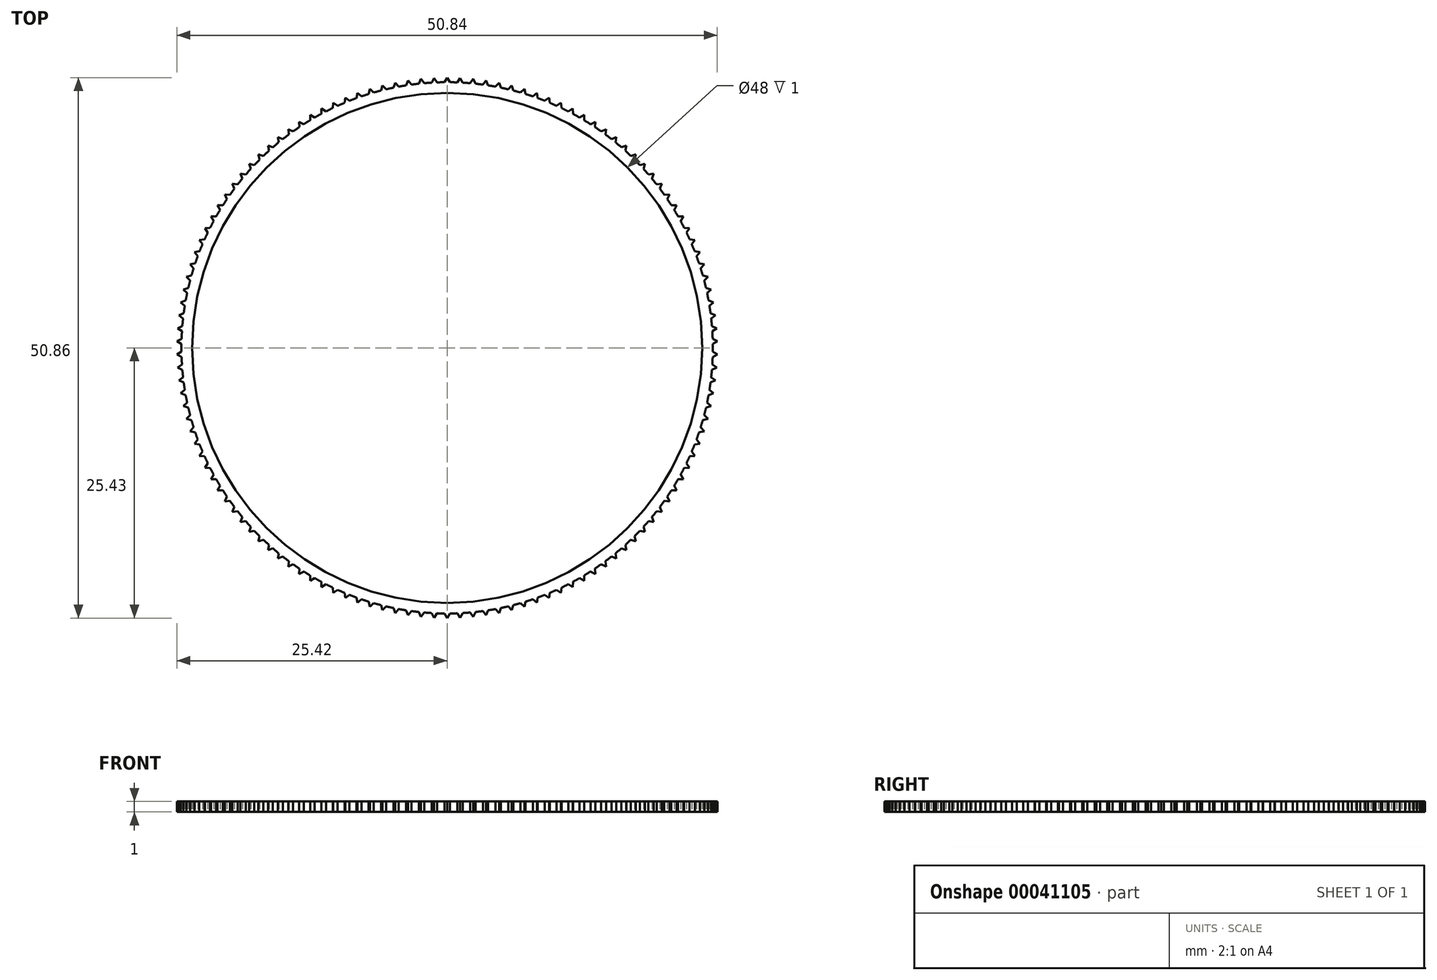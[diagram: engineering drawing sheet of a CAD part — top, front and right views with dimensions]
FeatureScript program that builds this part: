
annotation { "Feature Type Name" : "Feature", "Feature Type Description" : "" }
export const myFeature = defineFeature(function(context is Context, id is Id, definition is map)
    precondition{}
    {
        {
            var Q0;
            Q0=qCreatedBy(makeId("Top.planeOp"),FACE);
            var sketch = newSketch(context, id + "F0", { "sketchPlane" : qUnion([Q0])});
            skCircle(sketch, "E0", {"center": v(0, 0) * mm, "radius": 25 * mm});
            skLineSegment(sketch, "E1", {"start": v(0, 33.72) * mm, "end": v(0, -40.04) * mm, "construction": true});
            skLineSegment(sketch, "E2", {"start": v(-0.25, -25) * mm, "end": v(0, -25.43) * mm});
            skLineSegment(sketch, "E3", {"start": v(0, -25.43) * mm, "end": v(0.25, -25) * mm});
            skLineSegment(sketch, "E4", {"start": v(-0.25, -25) * mm, "end": v(0.25, -25) * mm, "construction": true});
            skLineSegment(sketch, "E5.1.0", {"start": v(0.96, -24.98) * mm, "end": v(1.23, -25.4) * mm});
            skLineSegment(sketch, "E5.1.1", {"start": v(1.23, -25.4) * mm, "end": v(1.46, -24.96) * mm});
            skLineSegment(sketch, "E5.2.0", {"start": v(2.16, -24.9) * mm, "end": v(2.45, -25.31) * mm});
            skLineSegment(sketch, "E5.2.1", {"start": v(2.45, -25.31) * mm, "end": v(2.66, -24.86) * mm});
            skLineSegment(sketch, "E5.3.0", {"start": v(3.36, -24.77) * mm, "end": v(3.67, -25.16) * mm});
            skLineSegment(sketch, "E5.3.1", {"start": v(3.67, -25.16) * mm, "end": v(3.86, -24.7) * mm});
            skLineSegment(sketch, "E5.4.0", {"start": v(4.56, -24.58) * mm, "end": v(4.89, -24.96) * mm});
            skLineSegment(sketch, "E5.4.1", {"start": v(4.89, -24.96) * mm, "end": v(5.05, -24.48) * mm});
            skLineSegment(sketch, "E5.5.0", {"start": v(5.74, -24.33) * mm, "end": v(6.09, -24.7) * mm});
            skLineSegment(sketch, "E5.5.1", {"start": v(6.09, -24.7) * mm, "end": v(6.23, -24.21) * mm});
            skLineSegment(sketch, "E5.6.0", {"start": v(6.9, -24.03) * mm, "end": v(7.27, -24.37) * mm});
            skLineSegment(sketch, "E5.6.1", {"start": v(7.27, -24.37) * mm, "end": v(7.39, -23.88) * mm});
            skLineSegment(sketch, "E5.7.0", {"start": v(8.06, -23.66) * mm, "end": v(8.44, -24) * mm});
            skLineSegment(sketch, "E5.7.1", {"start": v(8.44, -24) * mm, "end": v(8.53, -23.5) * mm});
            skLineSegment(sketch, "E5.8.0", {"start": v(9.2, -23.25) * mm, "end": v(9.6, -23.55) * mm});
            skLineSegment(sketch, "E5.8.1", {"start": v(9.6, -23.55) * mm, "end": v(9.66, -23.06) * mm});
            skLineSegment(sketch, "E5.9.0", {"start": v(10.3, -22.78) * mm, "end": v(10.72, -23.06) * mm});
            skLineSegment(sketch, "E5.9.1", {"start": v(10.72, -23.06) * mm, "end": v(10.76, -22.57) * mm});
            skLineSegment(sketch, "E5.10.0", {"start": v(11.4, -22.25) * mm, "end": v(11.82, -22.52) * mm});
            skLineSegment(sketch, "E5.10.1", {"start": v(11.82, -22.52) * mm, "end": v(11.84, -22.02) * mm});
            skLineSegment(sketch, "E5.11.0", {"start": v(12.46, -21.67) * mm, "end": v(12.9, -21.92) * mm});
            skLineSegment(sketch, "E5.11.1", {"start": v(12.9, -21.92) * mm, "end": v(12.89, -21.42) * mm});
            skLineSegment(sketch, "E5.12.0", {"start": v(13.5, -21.05) * mm, "end": v(13.94, -21.27) * mm});
            skLineSegment(sketch, "E5.12.1", {"start": v(13.94, -21.27) * mm, "end": v(13.9, -20.77) * mm});
            skLineSegment(sketch, "E5.13.0", {"start": v(14.5, -20.37) * mm, "end": v(14.95, -20.57) * mm});
            skLineSegment(sketch, "E5.13.1", {"start": v(14.95, -20.57) * mm, "end": v(14.9, -20.08) * mm});
            skLineSegment(sketch, "E5.14.0", {"start": v(15.46, -19.65) * mm, "end": v(15.92, -19.83) * mm});
            skLineSegment(sketch, "E5.14.1", {"start": v(15.92, -19.83) * mm, "end": v(15.85, -19.33) * mm});
            skLineSegment(sketch, "E5.15.0", {"start": v(16.4, -18.88) * mm, "end": v(16.86, -19.04) * mm});
            skLineSegment(sketch, "E5.15.1", {"start": v(16.86, -19.04) * mm, "end": v(16.76, -18.55) * mm});
            skLineSegment(sketch, "E5.16.0", {"start": v(17.28, -18.06) * mm, "end": v(17.76, -18.2) * mm});
            skLineSegment(sketch, "E5.16.1", {"start": v(17.76, -18.2) * mm, "end": v(17.64, -17.71) * mm});
            skLineSegment(sketch, "E5.17.0", {"start": v(18.14, -17.2) * mm, "end": v(18.62, -17.32) * mm});
            skLineSegment(sketch, "E5.17.1", {"start": v(18.62, -17.32) * mm, "end": v(18.48, -16.84) * mm});
            skLineSegment(sketch, "E5.18.0", {"start": v(18.95, -16.31) * mm, "end": v(19.44, -16.4) * mm});
            skLineSegment(sketch, "E5.18.1", {"start": v(19.44, -16.4) * mm, "end": v(19.27, -15.93) * mm});
            skLineSegment(sketch, "E5.19.0", {"start": v(19.71, -15.38) * mm, "end": v(20.2, -15.44) * mm});
            skLineSegment(sketch, "E5.19.1", {"start": v(20.2, -15.44) * mm, "end": v(20.02, -14.98) * mm});
            skLineSegment(sketch, "E5.20.0", {"start": v(20.43, -14.4) * mm, "end": v(20.93, -14.45) * mm});
            skLineSegment(sketch, "E5.20.1", {"start": v(20.93, -14.45) * mm, "end": v(20.72, -14) * mm});
            skLineSegment(sketch, "E5.21.0", {"start": v(21.1, -13.4) * mm, "end": v(21.6, -13.42) * mm});
            skLineSegment(sketch, "E5.21.1", {"start": v(21.6, -13.42) * mm, "end": v(21.37, -12.98) * mm});
            skLineSegment(sketch, "E5.22.0", {"start": v(21.73, -12.37) * mm, "end": v(22.23, -12.36) * mm});
            skLineSegment(sketch, "E5.22.1", {"start": v(22.23, -12.36) * mm, "end": v(21.97, -11.93) * mm});
            skLineSegment(sketch, "E5.23.0", {"start": v(22.3, -11.3) * mm, "end": v(22.8, -11.27) * mm});
            skLineSegment(sketch, "E5.23.1", {"start": v(22.8, -11.27) * mm, "end": v(22.52, -10.86) * mm});
            skLineSegment(sketch, "E5.24.0", {"start": v(22.82, -10.21) * mm, "end": v(23.32, -10.16) * mm});
            skLineSegment(sketch, "E5.24.1", {"start": v(23.32, -10.16) * mm, "end": v(23.02, -9.75) * mm});
            skLineSegment(sketch, "E5.25.0", {"start": v(23.29, -9.1) * mm, "end": v(23.78, -9.02) * mm});
            skLineSegment(sketch, "E5.25.1", {"start": v(23.78, -9.02) * mm, "end": v(23.46, -8.63) * mm});
            skLineSegment(sketch, "E5.26.0", {"start": v(23.7, -7.96) * mm, "end": v(24.19, -7.86) * mm});
            skLineSegment(sketch, "E5.26.1", {"start": v(24.19, -7.86) * mm, "end": v(23.85, -7.49) * mm});
            skLineSegment(sketch, "E5.27.0", {"start": v(24.06, -6.8) * mm, "end": v(24.54, -6.68) * mm});
            skLineSegment(sketch, "E5.27.1", {"start": v(24.54, -6.68) * mm, "end": v(24.19, -6.33) * mm});
            skLineSegment(sketch, "E5.28.0", {"start": v(24.36, -5.64) * mm, "end": v(24.83, -5.49) * mm});
            skLineSegment(sketch, "E5.28.1", {"start": v(24.83, -5.49) * mm, "end": v(24.46, -5.15) * mm});
            skLineSegment(sketch, "E5.29.0", {"start": v(24.6, -4.46) * mm, "end": v(25.07, -4.28) * mm});
            skLineSegment(sketch, "E5.29.1", {"start": v(25.07, -4.28) * mm, "end": v(24.68, -3.96) * mm});
            skLineSegment(sketch, "E5.30.0", {"start": v(24.79, -3.26) * mm, "end": v(25.25, -3.07) * mm});
            skLineSegment(sketch, "E5.30.1", {"start": v(25.25, -3.07) * mm, "end": v(24.85, -2.77) * mm});
            skLineSegment(sketch, "E5.31.0", {"start": v(24.91, -2.06) * mm, "end": v(25.36, -1.84) * mm});
            skLineSegment(sketch, "E5.31.1", {"start": v(25.36, -1.84) * mm, "end": v(24.95, -1.56) * mm});
            skLineSegment(sketch, "E5.32.0", {"start": v(24.99, -0.85) * mm, "end": v(25.42, -0.61) * mm});
            skLineSegment(sketch, "E5.32.1", {"start": v(25.42, -0.61) * mm, "end": v(25, -0.35) * mm});
            skLineSegment(sketch, "E5.33.0", {"start": v(25, 0.35) * mm, "end": v(25.42, 0.61) * mm});
            skLineSegment(sketch, "E5.33.1", {"start": v(25.42, 0.61) * mm, "end": v(24.99, 0.85) * mm});
            skLineSegment(sketch, "E5.34.0", {"start": v(24.95, 1.56) * mm, "end": v(25.36, 1.84) * mm});
            skLineSegment(sketch, "E5.34.1", {"start": v(25.36, 1.84) * mm, "end": v(24.91, 2.06) * mm});
            skLineSegment(sketch, "E5.35.0", {"start": v(24.85, 2.77) * mm, "end": v(25.25, 3.07) * mm});
            skLineSegment(sketch, "E5.35.1", {"start": v(25.25, 3.07) * mm, "end": v(24.79, 3.26) * mm});
            skLineSegment(sketch, "E5.36.0", {"start": v(24.68, 3.96) * mm, "end": v(25.07, 4.28) * mm});
            skLineSegment(sketch, "E5.36.1", {"start": v(25.07, 4.28) * mm, "end": v(24.6, 4.46) * mm});
            skLineSegment(sketch, "E5.37.0", {"start": v(24.46, 5.15) * mm, "end": v(24.83, 5.49) * mm});
            skLineSegment(sketch, "E5.37.1", {"start": v(24.83, 5.49) * mm, "end": v(24.36, 5.64) * mm});
            skLineSegment(sketch, "E5.38.0", {"start": v(24.19, 6.33) * mm, "end": v(24.54, 6.68) * mm});
            skLineSegment(sketch, "E5.38.1", {"start": v(24.54, 6.68) * mm, "end": v(24.06, 6.8) * mm});
            skLineSegment(sketch, "E5.39.0", {"start": v(23.85, 7.49) * mm, "end": v(24.19, 7.86) * mm});
            skLineSegment(sketch, "E5.39.1", {"start": v(24.19, 7.86) * mm, "end": v(23.7, 7.96) * mm});
            skLineSegment(sketch, "E5.40.0", {"start": v(23.46, 8.63) * mm, "end": v(23.78, 9.02) * mm});
            skLineSegment(sketch, "E5.40.1", {"start": v(23.78, 9.02) * mm, "end": v(23.29, 9.1) * mm});
            skLineSegment(sketch, "E5.41.0", {"start": v(23.02, 9.75) * mm, "end": v(23.32, 10.16) * mm});
            skLineSegment(sketch, "E5.41.1", {"start": v(23.32, 10.16) * mm, "end": v(22.82, 10.21) * mm});
            skLineSegment(sketch, "E5.42.0", {"start": v(22.52, 10.86) * mm, "end": v(22.8, 11.27) * mm});
            skLineSegment(sketch, "E5.42.1", {"start": v(22.8, 11.27) * mm, "end": v(22.3, 11.3) * mm});
            skLineSegment(sketch, "E5.43.0", {"start": v(21.97, 11.93) * mm, "end": v(22.23, 12.36) * mm});
            skLineSegment(sketch, "E5.43.1", {"start": v(22.23, 12.36) * mm, "end": v(21.73, 12.37) * mm});
            skLineSegment(sketch, "E5.44.0", {"start": v(21.37, 12.98) * mm, "end": v(21.6, 13.42) * mm});
            skLineSegment(sketch, "E5.44.1", {"start": v(21.6, 13.42) * mm, "end": v(21.1, 13.4) * mm});
            skLineSegment(sketch, "E5.45.0", {"start": v(20.72, 14) * mm, "end": v(20.93, 14.45) * mm});
            skLineSegment(sketch, "E5.45.1", {"start": v(20.93, 14.45) * mm, "end": v(20.43, 14.4) * mm});
            skLineSegment(sketch, "E5.46.0", {"start": v(20.02, 14.98) * mm, "end": v(20.2, 15.44) * mm});
            skLineSegment(sketch, "E5.46.1", {"start": v(20.2, 15.44) * mm, "end": v(19.71, 15.38) * mm});
            skLineSegment(sketch, "E5.47.0", {"start": v(19.27, 15.93) * mm, "end": v(19.44, 16.4) * mm});
            skLineSegment(sketch, "E5.47.1", {"start": v(19.44, 16.4) * mm, "end": v(18.95, 16.31) * mm});
            skLineSegment(sketch, "E5.48.0", {"start": v(18.48, 16.84) * mm, "end": v(18.62, 17.32) * mm});
            skLineSegment(sketch, "E5.48.1", {"start": v(18.62, 17.32) * mm, "end": v(18.14, 17.2) * mm});
            skLineSegment(sketch, "E5.49.0", {"start": v(17.64, 17.71) * mm, "end": v(17.76, 18.2) * mm});
            skLineSegment(sketch, "E5.49.1", {"start": v(17.76, 18.2) * mm, "end": v(17.28, 18.06) * mm});
            skLineSegment(sketch, "E5.50.0", {"start": v(16.76, 18.55) * mm, "end": v(16.86, 19.04) * mm});
            skLineSegment(sketch, "E5.50.1", {"start": v(16.86, 19.04) * mm, "end": v(16.4, 18.88) * mm});
            skLineSegment(sketch, "E5.51.0", {"start": v(15.85, 19.33) * mm, "end": v(15.92, 19.83) * mm});
            skLineSegment(sketch, "E5.51.1", {"start": v(15.92, 19.83) * mm, "end": v(15.46, 19.65) * mm});
            skLineSegment(sketch, "E5.52.0", {"start": v(14.9, 20.08) * mm, "end": v(14.95, 20.57) * mm});
            skLineSegment(sketch, "E5.52.1", {"start": v(14.95, 20.57) * mm, "end": v(14.5, 20.37) * mm});
            skLineSegment(sketch, "E5.53.0", {"start": v(13.9, 20.77) * mm, "end": v(13.94, 21.27) * mm});
            skLineSegment(sketch, "E5.53.1", {"start": v(13.94, 21.27) * mm, "end": v(13.5, 21.05) * mm});
            skLineSegment(sketch, "E5.54.0", {"start": v(12.89, 21.42) * mm, "end": v(12.9, 21.92) * mm});
            skLineSegment(sketch, "E5.54.1", {"start": v(12.9, 21.92) * mm, "end": v(12.46, 21.67) * mm});
            skLineSegment(sketch, "E5.55.0", {"start": v(11.84, 22.02) * mm, "end": v(11.82, 22.52) * mm});
            skLineSegment(sketch, "E5.55.1", {"start": v(11.82, 22.52) * mm, "end": v(11.4, 22.25) * mm});
            skLineSegment(sketch, "E5.56.0", {"start": v(10.76, 22.57) * mm, "end": v(10.72, 23.06) * mm});
            skLineSegment(sketch, "E5.56.1", {"start": v(10.72, 23.06) * mm, "end": v(10.3, 22.78) * mm});
            skLineSegment(sketch, "E5.57.0", {"start": v(9.66, 23.06) * mm, "end": v(9.6, 23.55) * mm});
            skLineSegment(sketch, "E5.57.1", {"start": v(9.6, 23.55) * mm, "end": v(9.2, 23.25) * mm});
            skLineSegment(sketch, "E5.58.0", {"start": v(8.53, 23.5) * mm, "end": v(8.44, 24) * mm});
            skLineSegment(sketch, "E5.58.1", {"start": v(8.44, 24) * mm, "end": v(8.06, 23.66) * mm});
            skLineSegment(sketch, "E5.59.0", {"start": v(7.39, 23.88) * mm, "end": v(7.27, 24.37) * mm});
            skLineSegment(sketch, "E5.59.1", {"start": v(7.27, 24.37) * mm, "end": v(6.9, 24.03) * mm});
            skLineSegment(sketch, "E5.60.0", {"start": v(6.23, 24.21) * mm, "end": v(6.09, 24.7) * mm});
            skLineSegment(sketch, "E5.60.1", {"start": v(6.09, 24.7) * mm, "end": v(5.74, 24.33) * mm});
            skLineSegment(sketch, "E5.61.0", {"start": v(5.05, 24.48) * mm, "end": v(4.89, 24.96) * mm});
            skLineSegment(sketch, "E5.61.1", {"start": v(4.89, 24.96) * mm, "end": v(4.56, 24.58) * mm});
            skLineSegment(sketch, "E5.62.0", {"start": v(3.86, 24.7) * mm, "end": v(3.67, 25.16) * mm});
            skLineSegment(sketch, "E5.62.1", {"start": v(3.67, 25.16) * mm, "end": v(3.36, 24.77) * mm});
            skLineSegment(sketch, "E5.63.0", {"start": v(2.66, 24.86) * mm, "end": v(2.45, 25.31) * mm});
            skLineSegment(sketch, "E5.63.1", {"start": v(2.45, 25.31) * mm, "end": v(2.16, 24.9) * mm});
            skLineSegment(sketch, "E5.64.0", {"start": v(1.46, 24.96) * mm, "end": v(1.23, 25.4) * mm});
            skLineSegment(sketch, "E5.64.1", {"start": v(1.23, 25.4) * mm, "end": v(0.96, 24.98) * mm});
            skLineSegment(sketch, "E5.65.0", {"start": v(0.25, 25) * mm, "end": v(0, 25.43) * mm});
            skLineSegment(sketch, "E5.65.1", {"start": v(0, 25.43) * mm, "end": v(-0.25, 25) * mm});
            skLineSegment(sketch, "E5.66.0", {"start": v(-0.96, 24.98) * mm, "end": v(-1.23, 25.4) * mm});
            skLineSegment(sketch, "E5.66.1", {"start": v(-1.23, 25.4) * mm, "end": v(-1.46, 24.96) * mm});
            skLineSegment(sketch, "E5.67.0", {"start": v(-2.16, 24.9) * mm, "end": v(-2.45, 25.31) * mm});
            skLineSegment(sketch, "E5.67.1", {"start": v(-2.45, 25.31) * mm, "end": v(-2.66, 24.86) * mm});
            skLineSegment(sketch, "E5.68.0", {"start": v(-3.36, 24.77) * mm, "end": v(-3.67, 25.16) * mm});
            skLineSegment(sketch, "E5.68.1", {"start": v(-3.67, 25.16) * mm, "end": v(-3.86, 24.7) * mm});
            skLineSegment(sketch, "E5.69.0", {"start": v(-4.56, 24.58) * mm, "end": v(-4.89, 24.96) * mm});
            skLineSegment(sketch, "E5.69.1", {"start": v(-4.89, 24.96) * mm, "end": v(-5.05, 24.48) * mm});
            skLineSegment(sketch, "E5.70.0", {"start": v(-5.74, 24.33) * mm, "end": v(-6.09, 24.7) * mm});
            skLineSegment(sketch, "E5.70.1", {"start": v(-6.09, 24.7) * mm, "end": v(-6.23, 24.21) * mm});
            skLineSegment(sketch, "E5.71.0", {"start": v(-6.9, 24.03) * mm, "end": v(-7.27, 24.37) * mm});
            skLineSegment(sketch, "E5.71.1", {"start": v(-7.27, 24.37) * mm, "end": v(-7.39, 23.88) * mm});
            skLineSegment(sketch, "E5.72.0", {"start": v(-8.06, 23.66) * mm, "end": v(-8.44, 24) * mm});
            skLineSegment(sketch, "E5.72.1", {"start": v(-8.44, 24) * mm, "end": v(-8.53, 23.5) * mm});
            skLineSegment(sketch, "E5.73.0", {"start": v(-9.2, 23.25) * mm, "end": v(-9.6, 23.55) * mm});
            skLineSegment(sketch, "E5.73.1", {"start": v(-9.6, 23.55) * mm, "end": v(-9.66, 23.06) * mm});
            skLineSegment(sketch, "E5.74.0", {"start": v(-10.3, 22.78) * mm, "end": v(-10.72, 23.06) * mm});
            skLineSegment(sketch, "E5.74.1", {"start": v(-10.72, 23.06) * mm, "end": v(-10.76, 22.57) * mm});
            skLineSegment(sketch, "E5.75.0", {"start": v(-11.4, 22.25) * mm, "end": v(-11.82, 22.52) * mm});
            skLineSegment(sketch, "E5.75.1", {"start": v(-11.82, 22.52) * mm, "end": v(-11.84, 22.02) * mm});
            skLineSegment(sketch, "E5.76.0", {"start": v(-12.46, 21.67) * mm, "end": v(-12.9, 21.92) * mm});
            skLineSegment(sketch, "E5.76.1", {"start": v(-12.9, 21.92) * mm, "end": v(-12.89, 21.42) * mm});
            skLineSegment(sketch, "E5.77.0", {"start": v(-13.5, 21.05) * mm, "end": v(-13.94, 21.27) * mm});
            skLineSegment(sketch, "E5.77.1", {"start": v(-13.94, 21.27) * mm, "end": v(-13.9, 20.77) * mm});
            skLineSegment(sketch, "E5.78.0", {"start": v(-14.5, 20.37) * mm, "end": v(-14.95, 20.57) * mm});
            skLineSegment(sketch, "E5.78.1", {"start": v(-14.95, 20.57) * mm, "end": v(-14.9, 20.08) * mm});
            skLineSegment(sketch, "E5.79.0", {"start": v(-15.46, 19.65) * mm, "end": v(-15.92, 19.83) * mm});
            skLineSegment(sketch, "E5.79.1", {"start": v(-15.92, 19.83) * mm, "end": v(-15.85, 19.33) * mm});
            skLineSegment(sketch, "E5.80.0", {"start": v(-16.4, 18.88) * mm, "end": v(-16.86, 19.04) * mm});
            skLineSegment(sketch, "E5.80.1", {"start": v(-16.86, 19.04) * mm, "end": v(-16.76, 18.55) * mm});
            skLineSegment(sketch, "E5.81.0", {"start": v(-17.28, 18.06) * mm, "end": v(-17.76, 18.2) * mm});
            skLineSegment(sketch, "E5.81.1", {"start": v(-17.76, 18.2) * mm, "end": v(-17.64, 17.71) * mm});
            skLineSegment(sketch, "E5.82.0", {"start": v(-18.14, 17.2) * mm, "end": v(-18.62, 17.32) * mm});
            skLineSegment(sketch, "E5.82.1", {"start": v(-18.62, 17.32) * mm, "end": v(-18.48, 16.84) * mm});
            skLineSegment(sketch, "E5.83.0", {"start": v(-18.95, 16.31) * mm, "end": v(-19.44, 16.4) * mm});
            skLineSegment(sketch, "E5.83.1", {"start": v(-19.44, 16.4) * mm, "end": v(-19.27, 15.93) * mm});
            skLineSegment(sketch, "E5.84.0", {"start": v(-19.71, 15.38) * mm, "end": v(-20.2, 15.44) * mm});
            skLineSegment(sketch, "E5.84.1", {"start": v(-20.2, 15.44) * mm, "end": v(-20.02, 14.98) * mm});
            skLineSegment(sketch, "E5.85.0", {"start": v(-20.43, 14.4) * mm, "end": v(-20.93, 14.45) * mm});
            skLineSegment(sketch, "E5.85.1", {"start": v(-20.93, 14.45) * mm, "end": v(-20.72, 14) * mm});
            skLineSegment(sketch, "E5.86.0", {"start": v(-21.1, 13.4) * mm, "end": v(-21.6, 13.42) * mm});
            skLineSegment(sketch, "E5.86.1", {"start": v(-21.6, 13.42) * mm, "end": v(-21.37, 12.98) * mm});
            skLineSegment(sketch, "E5.87.0", {"start": v(-21.73, 12.37) * mm, "end": v(-22.23, 12.36) * mm});
            skLineSegment(sketch, "E5.87.1", {"start": v(-22.23, 12.36) * mm, "end": v(-21.97, 11.93) * mm});
            skLineSegment(sketch, "E5.88.0", {"start": v(-22.3, 11.3) * mm, "end": v(-22.8, 11.27) * mm});
            skLineSegment(sketch, "E5.88.1", {"start": v(-22.8, 11.27) * mm, "end": v(-22.52, 10.86) * mm});
            skLineSegment(sketch, "E5.89.0", {"start": v(-22.82, 10.21) * mm, "end": v(-23.32, 10.16) * mm});
            skLineSegment(sketch, "E5.89.1", {"start": v(-23.32, 10.16) * mm, "end": v(-23.02, 9.75) * mm});
            skLineSegment(sketch, "E5.90.0", {"start": v(-23.29, 9.1) * mm, "end": v(-23.78, 9.02) * mm});
            skLineSegment(sketch, "E5.90.1", {"start": v(-23.78, 9.02) * mm, "end": v(-23.46, 8.63) * mm});
            skLineSegment(sketch, "E5.91.0", {"start": v(-23.7, 7.96) * mm, "end": v(-24.19, 7.86) * mm});
            skLineSegment(sketch, "E5.91.1", {"start": v(-24.19, 7.86) * mm, "end": v(-23.85, 7.49) * mm});
            skLineSegment(sketch, "E5.92.0", {"start": v(-24.06, 6.8) * mm, "end": v(-24.54, 6.68) * mm});
            skLineSegment(sketch, "E5.92.1", {"start": v(-24.54, 6.68) * mm, "end": v(-24.19, 6.33) * mm});
            skLineSegment(sketch, "E5.93.0", {"start": v(-24.36, 5.64) * mm, "end": v(-24.83, 5.49) * mm});
            skLineSegment(sketch, "E5.93.1", {"start": v(-24.83, 5.49) * mm, "end": v(-24.46, 5.15) * mm});
            skLineSegment(sketch, "E5.94.0", {"start": v(-24.6, 4.46) * mm, "end": v(-25.07, 4.28) * mm});
            skLineSegment(sketch, "E5.94.1", {"start": v(-25.07, 4.28) * mm, "end": v(-24.68, 3.96) * mm});
            skLineSegment(sketch, "E5.95.0", {"start": v(-24.79, 3.26) * mm, "end": v(-25.25, 3.07) * mm});
            skLineSegment(sketch, "E5.95.1", {"start": v(-25.25, 3.07) * mm, "end": v(-24.85, 2.77) * mm});
            skLineSegment(sketch, "E5.96.0", {"start": v(-24.91, 2.06) * mm, "end": v(-25.36, 1.84) * mm});
            skLineSegment(sketch, "E5.96.1", {"start": v(-25.36, 1.84) * mm, "end": v(-24.95, 1.56) * mm});
            skLineSegment(sketch, "E5.97.0", {"start": v(-24.99, 0.85) * mm, "end": v(-25.42, 0.61) * mm});
            skLineSegment(sketch, "E5.97.1", {"start": v(-25.42, 0.61) * mm, "end": v(-25, 0.35) * mm});
            skLineSegment(sketch, "E5.98.0", {"start": v(-25, -0.35) * mm, "end": v(-25.42, -0.61) * mm});
            skLineSegment(sketch, "E5.98.1", {"start": v(-25.42, -0.61) * mm, "end": v(-24.99, -0.85) * mm});
            skLineSegment(sketch, "E5.99.0", {"start": v(-24.95, -1.56) * mm, "end": v(-25.36, -1.84) * mm});
            skLineSegment(sketch, "E5.99.1", {"start": v(-25.36, -1.84) * mm, "end": v(-24.91, -2.06) * mm});
            skCircle(sketch, "E6.0", {"center": v(0, 0) * mm, "radius": 24 * mm});
            skLineSegment(sketch, "E7.2.100.0", {"start": v(-24.85, -2.77) * mm, "end": v(-25.25, -3.07) * mm});
            skLineSegment(sketch, "E7.3.100.0", {"start": v(-25.25, -3.07) * mm, "end": v(-24.79, -3.26) * mm});
            skLineSegment(sketch, "E7.2.101.0", {"start": v(-24.68, -3.96) * mm, "end": v(-25.07, -4.28) * mm});
            skLineSegment(sketch, "E7.3.101.0", {"start": v(-25.07, -4.28) * mm, "end": v(-24.6, -4.46) * mm});
            skLineSegment(sketch, "E7.2.102.0", {"start": v(-24.46, -5.15) * mm, "end": v(-24.83, -5.49) * mm});
            skLineSegment(sketch, "E7.3.102.0", {"start": v(-24.83, -5.49) * mm, "end": v(-24.36, -5.64) * mm});
            skLineSegment(sketch, "E7.2.103.0", {"start": v(-24.19, -6.33) * mm, "end": v(-24.54, -6.68) * mm});
            skLineSegment(sketch, "E7.3.103.0", {"start": v(-24.54, -6.68) * mm, "end": v(-24.06, -6.8) * mm});
            skLineSegment(sketch, "E7.2.104.0", {"start": v(-23.85, -7.49) * mm, "end": v(-24.19, -7.86) * mm});
            skLineSegment(sketch, "E7.3.104.0", {"start": v(-24.19, -7.86) * mm, "end": v(-23.7, -7.96) * mm});
            skLineSegment(sketch, "E7.2.105.0", {"start": v(-23.46, -8.63) * mm, "end": v(-23.78, -9.02) * mm});
            skLineSegment(sketch, "E7.3.105.0", {"start": v(-23.78, -9.02) * mm, "end": v(-23.29, -9.1) * mm});
            skLineSegment(sketch, "E7.2.106.0", {"start": v(-23.02, -9.75) * mm, "end": v(-23.32, -10.16) * mm});
            skLineSegment(sketch, "E7.3.106.0", {"start": v(-23.32, -10.16) * mm, "end": v(-22.82, -10.21) * mm});
            skLineSegment(sketch, "E7.2.107.0", {"start": v(-22.52, -10.86) * mm, "end": v(-22.8, -11.27) * mm});
            skLineSegment(sketch, "E7.3.107.0", {"start": v(-22.8, -11.27) * mm, "end": v(-22.3, -11.3) * mm});
            skLineSegment(sketch, "E7.2.108.0", {"start": v(-21.97, -11.93) * mm, "end": v(-22.23, -12.36) * mm});
            skLineSegment(sketch, "E7.3.108.0", {"start": v(-22.23, -12.36) * mm, "end": v(-21.73, -12.37) * mm});
            skLineSegment(sketch, "E7.2.109.0", {"start": v(-21.37, -12.98) * mm, "end": v(-21.6, -13.42) * mm});
            skLineSegment(sketch, "E7.3.109.0", {"start": v(-21.6, -13.42) * mm, "end": v(-21.1, -13.4) * mm});
            skLineSegment(sketch, "E7.2.110.0", {"start": v(-20.72, -14) * mm, "end": v(-20.93, -14.45) * mm});
            skLineSegment(sketch, "E7.3.110.0", {"start": v(-20.93, -14.45) * mm, "end": v(-20.43, -14.4) * mm});
            skLineSegment(sketch, "E7.2.111.0", {"start": v(-20.02, -14.98) * mm, "end": v(-20.2, -15.44) * mm});
            skLineSegment(sketch, "E7.3.111.0", {"start": v(-20.2, -15.44) * mm, "end": v(-19.71, -15.38) * mm});
            skLineSegment(sketch, "E7.2.112.0", {"start": v(-19.27, -15.93) * mm, "end": v(-19.44, -16.4) * mm});
            skLineSegment(sketch, "E7.3.112.0", {"start": v(-19.44, -16.4) * mm, "end": v(-18.95, -16.31) * mm});
            skLineSegment(sketch, "E7.2.113.0", {"start": v(-18.48, -16.84) * mm, "end": v(-18.62, -17.32) * mm});
            skLineSegment(sketch, "E7.3.113.0", {"start": v(-18.62, -17.32) * mm, "end": v(-18.14, -17.2) * mm});
            skLineSegment(sketch, "E7.2.114.0", {"start": v(-17.64, -17.71) * mm, "end": v(-17.76, -18.2) * mm});
            skLineSegment(sketch, "E7.3.114.0", {"start": v(-17.76, -18.2) * mm, "end": v(-17.28, -18.06) * mm});
            skLineSegment(sketch, "E7.2.115.0", {"start": v(-16.76, -18.55) * mm, "end": v(-16.86, -19.04) * mm});
            skLineSegment(sketch, "E7.3.115.0", {"start": v(-16.86, -19.04) * mm, "end": v(-16.4, -18.88) * mm});
            skLineSegment(sketch, "E7.2.116.0", {"start": v(-15.85, -19.33) * mm, "end": v(-15.92, -19.83) * mm});
            skLineSegment(sketch, "E7.3.116.0", {"start": v(-15.92, -19.83) * mm, "end": v(-15.46, -19.65) * mm});
            skLineSegment(sketch, "E7.2.117.0", {"start": v(-14.9, -20.08) * mm, "end": v(-14.95, -20.57) * mm});
            skLineSegment(sketch, "E7.3.117.0", {"start": v(-14.95, -20.57) * mm, "end": v(-14.5, -20.37) * mm});
            skLineSegment(sketch, "E7.2.118.0", {"start": v(-13.9, -20.77) * mm, "end": v(-13.94, -21.27) * mm});
            skLineSegment(sketch, "E7.3.118.0", {"start": v(-13.94, -21.27) * mm, "end": v(-13.5, -21.05) * mm});
            skLineSegment(sketch, "E7.2.119.0", {"start": v(-12.89, -21.42) * mm, "end": v(-12.9, -21.92) * mm});
            skLineSegment(sketch, "E7.3.119.0", {"start": v(-12.9, -21.92) * mm, "end": v(-12.46, -21.67) * mm});
            skLineSegment(sketch, "E7.2.120.0", {"start": v(-11.84, -22.02) * mm, "end": v(-11.82, -22.52) * mm});
            skLineSegment(sketch, "E7.3.120.0", {"start": v(-11.82, -22.52) * mm, "end": v(-11.4, -22.25) * mm});
            skLineSegment(sketch, "E7.2.121.0", {"start": v(-10.76, -22.57) * mm, "end": v(-10.72, -23.06) * mm});
            skLineSegment(sketch, "E7.3.121.0", {"start": v(-10.72, -23.06) * mm, "end": v(-10.3, -22.78) * mm});
            skLineSegment(sketch, "E7.2.122.0", {"start": v(-9.66, -23.06) * mm, "end": v(-9.6, -23.55) * mm});
            skLineSegment(sketch, "E7.3.122.0", {"start": v(-9.6, -23.55) * mm, "end": v(-9.2, -23.25) * mm});
            skLineSegment(sketch, "E7.2.123.0", {"start": v(-8.53, -23.5) * mm, "end": v(-8.44, -24) * mm});
            skLineSegment(sketch, "E7.3.123.0", {"start": v(-8.44, -24) * mm, "end": v(-8.06, -23.66) * mm});
            skLineSegment(sketch, "E7.2.124.0", {"start": v(-7.39, -23.88) * mm, "end": v(-7.27, -24.37) * mm});
            skLineSegment(sketch, "E7.3.124.0", {"start": v(-7.27, -24.37) * mm, "end": v(-6.9, -24.03) * mm});
            skLineSegment(sketch, "E7.2.125.0", {"start": v(-6.23, -24.21) * mm, "end": v(-6.09, -24.7) * mm});
            skLineSegment(sketch, "E7.3.125.0", {"start": v(-6.09, -24.7) * mm, "end": v(-5.74, -24.33) * mm});
            skLineSegment(sketch, "E7.2.126.0", {"start": v(-5.05, -24.48) * mm, "end": v(-4.89, -24.96) * mm});
            skLineSegment(sketch, "E7.3.126.0", {"start": v(-4.89, -24.96) * mm, "end": v(-4.56, -24.58) * mm});
            skLineSegment(sketch, "E7.2.127.0", {"start": v(-3.86, -24.7) * mm, "end": v(-3.67, -25.16) * mm});
            skLineSegment(sketch, "E7.3.127.0", {"start": v(-3.67, -25.16) * mm, "end": v(-3.36, -24.77) * mm});
            skLineSegment(sketch, "E7.2.128.0", {"start": v(-2.66, -24.86) * mm, "end": v(-2.45, -25.31) * mm});
            skLineSegment(sketch, "E7.3.128.0", {"start": v(-2.45, -25.31) * mm, "end": v(-2.16, -24.9) * mm});
            skLineSegment(sketch, "E7.2.129.0", {"start": v(-1.46, -24.96) * mm, "end": v(-1.23, -25.4) * mm});
            skLineSegment(sketch, "E7.3.129.0", {"start": v(-1.23, -25.4) * mm, "end": v(-0.96, -24.98) * mm});
            skSolve(sketch);
        }
        {
            var Q0;
            Q0=makeQuery(id+"F0.imprint","IMPRINT",FACE,{"disambiguationData":[TD([[makeQuery(id+"F0.imprint","IMPRINT",EDGE,{"derivedFrom":sQuery(id+"F0.wireOp",EDGE,"E6.0")}),-1.0]])]});
            var Q1;
            {var subQ1=sQuery(id+"F0.wireOp",EDGE,"E5.84.0");Q1=makeQuery(id+"F0.imprint","IMPRINT",FACE,{"disambiguationData":[TD([[makeQuery(id+"F0.imprint","IMPRINT",EDGE,{"derivedFrom":subQ1}),1.0]])]});}
            var Q2;
            {var subQ1=sQuery(id+"F0.wireOp",EDGE,"E5.52.0");Q2=makeQuery(id+"F0.imprint","IMPRINT",FACE,{"disambiguationData":[TD([[makeQuery(id+"F0.imprint","IMPRINT",EDGE,{"derivedFrom":subQ1}),1.0]])]});}
            var Q3;
            {var subQ1=sQuery(id+"F0.wireOp",EDGE,"E7.2.115.0");Q3=makeQuery(id+"F0.imprint","IMPRINT",FACE,{"disambiguationData":[TD([[makeQuery(id+"F0.imprint","IMPRINT",EDGE,{"derivedFrom":subQ1}),1.0]])]});}
            var Q4;
            {var subQ1=sQuery(id+"F0.wireOp",EDGE,"E5.51.0");Q4=makeQuery(id+"F0.imprint","IMPRINT",FACE,{"disambiguationData":[TD([[makeQuery(id+"F0.imprint","IMPRINT",EDGE,{"derivedFrom":subQ1}),1.0]])]});}
            var Q5;
            {var subQ1=sQuery(id+"F0.wireOp",EDGE,"E5.16.0");Q5=makeQuery(id+"F0.imprint","IMPRINT",FACE,{"disambiguationData":[TD([[makeQuery(id+"F0.imprint","IMPRINT",EDGE,{"derivedFrom":subQ1}),1.0]])]});}
            var Q6;
            {var subQ0=sQuery(id+"F0.wireOp",EDGE,"E7.2.114.0");Q6=makeQuery(id+"F0.imprint","IMPRINT",FACE,{"disambiguationData":[TD([[makeQuery(id+"F0.imprint","IMPRINT",EDGE,{"derivedFrom":subQ0}),1.0]])]});}
            var Q7;
            {var subQ1=sQuery(id+"F0.wireOp",EDGE,"E5.15.0");Q7=makeQuery(id+"F0.imprint","IMPRINT",FACE,{"disambiguationData":[TD([[makeQuery(id+"F0.imprint","IMPRINT",EDGE,{"derivedFrom":subQ1}),1.0]])]});}
            var Q8;
            {var subQ1=sQuery(id+"F0.wireOp",EDGE,"E5.79.0");Q8=makeQuery(id+"F0.imprint","IMPRINT",FACE,{"disambiguationData":[TD([[makeQuery(id+"F0.imprint","IMPRINT",EDGE,{"derivedFrom":subQ1}),1.0]])]});}
            var Q9;
            {var subQ1=sQuery(id+"F0.wireOp",EDGE,"E5.12.0");Q9=makeQuery(id+"F0.imprint","IMPRINT",FACE,{"disambiguationData":[TD([[makeQuery(id+"F0.imprint","IMPRINT",EDGE,{"derivedFrom":subQ1}),1.0]])]});}
            var Q10;
            {var subQ1=sQuery(id+"F0.wireOp",EDGE,"E5.78.0");Q10=makeQuery(id+"F0.imprint","IMPRINT",FACE,{"disambiguationData":[TD([[makeQuery(id+"F0.imprint","IMPRINT",EDGE,{"derivedFrom":subQ1}),1.0]])]});}
            var Q11;
            {var subQ1=sQuery(id+"F0.wireOp",EDGE,"E7.2.118.0");Q11=makeQuery(id+"F0.imprint","IMPRINT",FACE,{"disambiguationData":[TD([[makeQuery(id+"F0.imprint","IMPRINT",EDGE,{"derivedFrom":subQ1}),1.0]])]});}
            var Q12;
            {var subQ1=sQuery(id+"F0.wireOp",EDGE,"E5.87.0");Q12=makeQuery(id+"F0.imprint","IMPRINT",FACE,{"disambiguationData":[TD([[makeQuery(id+"F0.imprint","IMPRINT",EDGE,{"derivedFrom":subQ1}),1.0]])]});}
            var Q13;
            {var subQ1=sQuery(id+"F0.wireOp",EDGE,"E5.46.0");Q13=makeQuery(id+"F0.imprint","IMPRINT",FACE,{"disambiguationData":[TD([[makeQuery(id+"F0.imprint","IMPRINT",EDGE,{"derivedFrom":subQ1}),1.0]])]});}
            var Q14;
            {var subQ0=sQuery(id+"F0.wireOp",EDGE,"E5.43.0");Q14=makeQuery(id+"F0.imprint","IMPRINT",FACE,{"disambiguationData":[TD([[makeQuery(id+"F0.imprint","IMPRINT",EDGE,{"derivedFrom":subQ0}),1.0]])]});}
            var Q15;
            {var subQ1=sQuery(id+"F0.wireOp",EDGE,"E7.2.104.0");Q15=makeQuery(id+"F0.imprint","IMPRINT",FACE,{"disambiguationData":[TD([[makeQuery(id+"F0.imprint","IMPRINT",EDGE,{"derivedFrom":subQ1}),1.0]])]});}
            var Q16;
            {var subQ1=sQuery(id+"F0.wireOp",EDGE,"E5.50.0");Q16=makeQuery(id+"F0.imprint","IMPRINT",FACE,{"disambiguationData":[TD([[makeQuery(id+"F0.imprint","IMPRINT",EDGE,{"derivedFrom":subQ1}),1.0]])]});}
            var Q17;
            {var subQ1=sQuery(id+"F0.wireOp",EDGE,"E5.80.0");Q17=makeQuery(id+"F0.imprint","IMPRINT",FACE,{"disambiguationData":[TD([[makeQuery(id+"F0.imprint","IMPRINT",EDGE,{"derivedFrom":subQ1}),1.0]])]});}
            var Q18;
            {var subQ1=sQuery(id+"F0.wireOp",EDGE,"E7.2.108.0");Q18=makeQuery(id+"F0.imprint","IMPRINT",FACE,{"disambiguationData":[TD([[makeQuery(id+"F0.imprint","IMPRINT",EDGE,{"derivedFrom":subQ1}),1.0]])]});}
            var Q19;
            {var subQ1=sQuery(id+"F0.wireOp",EDGE,"E5.26.0");Q19=makeQuery(id+"F0.imprint","IMPRINT",FACE,{"disambiguationData":[TD([[makeQuery(id+"F0.imprint","IMPRINT",EDGE,{"derivedFrom":subQ1}),1.0]])]});}
            var Q20;
            {var subQ1=sQuery(id+"F0.wireOp",EDGE,"E5.47.0");Q20=makeQuery(id+"F0.imprint","IMPRINT",FACE,{"disambiguationData":[TD([[makeQuery(id+"F0.imprint","IMPRINT",EDGE,{"derivedFrom":subQ1}),1.0]])]});}
            var Q21;
            {var subQ0=sQuery(id+"F0.wireOp",EDGE,"E5.41.0");Q21=makeQuery(id+"F0.imprint","IMPRINT",FACE,{"disambiguationData":[TD([[makeQuery(id+"F0.imprint","IMPRINT",EDGE,{"derivedFrom":subQ0}),1.0]])]});}
            var Q22;
            {var subQ1=sQuery(id+"F0.wireOp",EDGE,"E5.72.0");Q22=makeQuery(id+"F0.imprint","IMPRINT",FACE,{"disambiguationData":[TD([[makeQuery(id+"F0.imprint","IMPRINT",EDGE,{"derivedFrom":subQ1}),1.0]])]});}
            var Q23;
            {var subQ1=sQuery(id+"F0.wireOp",EDGE,"E5.56.0");Q23=makeQuery(id+"F0.imprint","IMPRINT",FACE,{"disambiguationData":[TD([[makeQuery(id+"F0.imprint","IMPRINT",EDGE,{"derivedFrom":subQ1}),1.0]])]});}
            var Q24;
            {var subQ1=sQuery(id+"F0.wireOp",EDGE,"E7.2.120.0");Q24=makeQuery(id+"F0.imprint","IMPRINT",FACE,{"disambiguationData":[TD([[makeQuery(id+"F0.imprint","IMPRINT",EDGE,{"derivedFrom":subQ1}),1.0]])]});}
            var Q25;
            {var subQ0=sQuery(id+"F0.wireOp",EDGE,"E5.58.0");Q25=makeQuery(id+"F0.imprint","IMPRINT",FACE,{"disambiguationData":[TD([[makeQuery(id+"F0.imprint","IMPRINT",EDGE,{"derivedFrom":subQ0}),1.0]])]});}
            var Q26;
            {var subQ1=sQuery(id+"F0.wireOp",EDGE,"E7.2.122.0");Q26=makeQuery(id+"F0.imprint","IMPRINT",FACE,{"disambiguationData":[TD([[makeQuery(id+"F0.imprint","IMPRINT",EDGE,{"derivedFrom":subQ1}),1.0]])]});}
            var Q27;
            {var subQ0=sQuery(id+"F0.wireOp",EDGE,"E5.24.0");Q27=makeQuery(id+"F0.imprint","IMPRINT",FACE,{"disambiguationData":[TD([[makeQuery(id+"F0.imprint","IMPRINT",EDGE,{"derivedFrom":subQ0}),1.0]])]});}
            var Q28;
            {var subQ1=sQuery(id+"F0.wireOp",EDGE,"E7.2.106.0");Q28=makeQuery(id+"F0.imprint","IMPRINT",FACE,{"disambiguationData":[TD([[makeQuery(id+"F0.imprint","IMPRINT",EDGE,{"derivedFrom":subQ1}),1.0]])]});}
            var Q29;
            {var subQ1=sQuery(id+"F0.wireOp",EDGE,"E5.18.0");Q29=makeQuery(id+"F0.imprint","IMPRINT",FACE,{"disambiguationData":[TD([[makeQuery(id+"F0.imprint","IMPRINT",EDGE,{"derivedFrom":subQ1}),1.0]])]});}
            var Q30;
            {var subQ1=sQuery(id+"F0.wireOp",EDGE,"E5.17.0");Q30=makeQuery(id+"F0.imprint","IMPRINT",FACE,{"disambiguationData":[TD([[makeQuery(id+"F0.imprint","IMPRINT",EDGE,{"derivedFrom":subQ1}),1.0]])]});}
            var Q31;
            {var subQ1=sQuery(id+"F0.wireOp",EDGE,"E5.81.0");Q31=makeQuery(id+"F0.imprint","IMPRINT",FACE,{"disambiguationData":[TD([[makeQuery(id+"F0.imprint","IMPRINT",EDGE,{"derivedFrom":subQ1}),1.0]])]});}
            var Q32;
            {var subQ1=sQuery(id+"F0.wireOp",EDGE,"E7.2.127.0");Q32=makeQuery(id+"F0.imprint","IMPRINT",FACE,{"disambiguationData":[TD([[makeQuery(id+"F0.imprint","IMPRINT",EDGE,{"derivedFrom":subQ1}),1.0]])]});}
            var Q33;
            {var subQ1=sQuery(id+"F0.wireOp",EDGE,"E7.2.128.0");Q33=makeQuery(id+"F0.imprint","IMPRINT",FACE,{"disambiguationData":[TD([[makeQuery(id+"F0.imprint","IMPRINT",EDGE,{"derivedFrom":subQ1}),1.0]])]});}
            var Q34;
            {var subQ1=sQuery(id+"F0.wireOp",EDGE,"E5.27.0");Q34=makeQuery(id+"F0.imprint","IMPRINT",FACE,{"disambiguationData":[TD([[makeQuery(id+"F0.imprint","IMPRINT",EDGE,{"derivedFrom":subQ1}),1.0]])]});}
            var Q35;
            {var subQ1=sQuery(id+"F0.wireOp",EDGE,"E5.76.0");Q35=makeQuery(id+"F0.imprint","IMPRINT",FACE,{"disambiguationData":[TD([[makeQuery(id+"F0.imprint","IMPRINT",EDGE,{"derivedFrom":subQ1}),1.0]])]});}
            var Q36;
            {var subQ0=sQuery(id+"F0.wireOp",EDGE,"E5.54.0");Q36=makeQuery(id+"F0.imprint","IMPRINT",FACE,{"disambiguationData":[TD([[makeQuery(id+"F0.imprint","IMPRINT",EDGE,{"derivedFrom":subQ0}),1.0]])]});}
            var Q37;
            {var subQ1=sQuery(id+"F0.wireOp",EDGE,"E5.20.0");Q37=makeQuery(id+"F0.imprint","IMPRINT",FACE,{"disambiguationData":[TD([[makeQuery(id+"F0.imprint","IMPRINT",EDGE,{"derivedFrom":subQ1}),1.0]])]});}
            var Q38;
            {var subQ1=sQuery(id+"F0.wireOp",EDGE,"E5.36.0");Q38=makeQuery(id+"F0.imprint","IMPRINT",FACE,{"disambiguationData":[TD([[makeQuery(id+"F0.imprint","IMPRINT",EDGE,{"derivedFrom":subQ1}),1.0]])]});}
            var Q39;
            {var subQ1=sQuery(id+"F0.wireOp",EDGE,"E5.38.0");Q39=makeQuery(id+"F0.imprint","IMPRINT",FACE,{"disambiguationData":[TD([[makeQuery(id+"F0.imprint","IMPRINT",EDGE,{"derivedFrom":subQ1}),1.0]])]});}
            var Q40;
            {var subQ1=sQuery(id+"F0.wireOp",EDGE,"E5.89.0");Q40=makeQuery(id+"F0.imprint","IMPRINT",FACE,{"disambiguationData":[TD([[makeQuery(id+"F0.imprint","IMPRINT",EDGE,{"derivedFrom":subQ1}),1.0]])]});}
            var Q41;
            {var subQ1=sQuery(id+"F0.wireOp",EDGE,"E7.2.117.0");Q41=makeQuery(id+"F0.imprint","IMPRINT",FACE,{"disambiguationData":[TD([[makeQuery(id+"F0.imprint","IMPRINT",EDGE,{"derivedFrom":subQ1}),1.0]])]});}
            var Q42;
            {var subQ1=sQuery(id+"F0.wireOp",EDGE,"E5.53.0");Q42=makeQuery(id+"F0.imprint","IMPRINT",FACE,{"disambiguationData":[TD([[makeQuery(id+"F0.imprint","IMPRINT",EDGE,{"derivedFrom":subQ1}),1.0]])]});}
            var Q43;
            {var subQ1=sQuery(id+"F0.wireOp",EDGE,"E5.68.0");Q43=makeQuery(id+"F0.imprint","IMPRINT",FACE,{"disambiguationData":[TD([[makeQuery(id+"F0.imprint","IMPRINT",EDGE,{"derivedFrom":subQ1}),1.0]])]});}
            var Q44;
            {var subQ0=sQuery(id+"F0.wireOp",EDGE,"E7.2.129.0");Q44=makeQuery(id+"F0.imprint","IMPRINT",FACE,{"disambiguationData":[TD([[makeQuery(id+"F0.imprint","IMPRINT",EDGE,{"derivedFrom":subQ0}),1.0]])]});}
            var Q45;
            {var subQ1=sQuery(id+"F0.wireOp",EDGE,"E5.95.0");Q45=makeQuery(id+"F0.imprint","IMPRINT",FACE,{"disambiguationData":[TD([[makeQuery(id+"F0.imprint","IMPRINT",EDGE,{"derivedFrom":subQ1}),1.0]])]});}
            var Q46;
            {var subQ1=sQuery(id+"F0.wireOp",EDGE,"E7.2.111.0");Q46=makeQuery(id+"F0.imprint","IMPRINT",FACE,{"disambiguationData":[TD([[makeQuery(id+"F0.imprint","IMPRINT",EDGE,{"derivedFrom":subQ1}),1.0]])]});}
            var Q47;
            {var subQ1=sQuery(id+"F0.wireOp",EDGE,"E5.94.0");Q47=makeQuery(id+"F0.imprint","IMPRINT",FACE,{"disambiguationData":[TD([[makeQuery(id+"F0.imprint","IMPRINT",EDGE,{"derivedFrom":subQ1}),1.0]])]});}
            var Q48;
            {var subQ1=sQuery(id+"F0.wireOp",EDGE,"E7.2.112.0");Q48=makeQuery(id+"F0.imprint","IMPRINT",FACE,{"disambiguationData":[TD([[makeQuery(id+"F0.imprint","IMPRINT",EDGE,{"derivedFrom":subQ1}),1.0]])]});}
            var Q49;
            {var subQ1=sQuery(id+"F0.wireOp",EDGE,"E5.61.0");Q49=makeQuery(id+"F0.imprint","IMPRINT",FACE,{"disambiguationData":[TD([[makeQuery(id+"F0.imprint","IMPRINT",EDGE,{"derivedFrom":subQ1}),1.0]])]});}
            var Q50;
            {var subQ1=sQuery(id+"F0.wireOp",EDGE,"E5.25.0");Q50=makeQuery(id+"F0.imprint","IMPRINT",FACE,{"disambiguationData":[TD([[makeQuery(id+"F0.imprint","IMPRINT",EDGE,{"derivedFrom":subQ1}),1.0]])]});}
            var Q51;
            {var subQ1=sQuery(id+"F0.wireOp",EDGE,"E5.35.0");Q51=makeQuery(id+"F0.imprint","IMPRINT",FACE,{"disambiguationData":[TD([[makeQuery(id+"F0.imprint","IMPRINT",EDGE,{"derivedFrom":subQ1}),1.0]])]});}
            var Q52;
            {var subQ1=sQuery(id+"F0.wireOp",EDGE,"E5.8.0");Q52=makeQuery(id+"F0.imprint","IMPRINT",FACE,{"disambiguationData":[TD([[makeQuery(id+"F0.imprint","IMPRINT",EDGE,{"derivedFrom":subQ1}),1.0]])]});}
            var Q53;
            {var subQ1=sQuery(id+"F0.wireOp",EDGE,"E5.69.0");Q53=makeQuery(id+"F0.imprint","IMPRINT",FACE,{"disambiguationData":[TD([[makeQuery(id+"F0.imprint","IMPRINT",EDGE,{"derivedFrom":subQ1}),1.0]])]});}
            var Q54;
            {var subQ1=sQuery(id+"F0.wireOp",EDGE,"E5.2.0");Q54=makeQuery(id+"F0.imprint","IMPRINT",FACE,{"disambiguationData":[TD([[makeQuery(id+"F0.imprint","IMPRINT",EDGE,{"derivedFrom":subQ1}),1.0]])]});}
            var Q55;
            {var subQ1=sQuery(id+"F0.wireOp",EDGE,"E5.1.0");Q55=makeQuery(id+"F0.imprint","IMPRINT",FACE,{"disambiguationData":[TD([[makeQuery(id+"F0.imprint","IMPRINT",EDGE,{"derivedFrom":subQ1}),1.0]])]});}
            var Q56;
            {var subQ1=sQuery(id+"F0.wireOp",EDGE,"E5.63.0");Q56=makeQuery(id+"F0.imprint","IMPRINT",FACE,{"disambiguationData":[TD([[makeQuery(id+"F0.imprint","IMPRINT",EDGE,{"derivedFrom":subQ1}),1.0]])]});}
            var Q57;
            {var subQ1=sQuery(id+"F0.wireOp",EDGE,"E5.62.0");Q57=makeQuery(id+"F0.imprint","IMPRINT",FACE,{"disambiguationData":[TD([[makeQuery(id+"F0.imprint","IMPRINT",EDGE,{"derivedFrom":subQ1}),1.0]])]});}
            var Q58;
            {var subQ1=sQuery(id+"F0.wireOp",EDGE,"E5.3.0");Q58=makeQuery(id+"F0.imprint","IMPRINT",FACE,{"disambiguationData":[TD([[makeQuery(id+"F0.imprint","IMPRINT",EDGE,{"derivedFrom":subQ1}),1.0]])]});}
            var Q59;
            {var subQ1=sQuery(id+"F0.wireOp",EDGE,"E7.2.100.0");Q59=makeQuery(id+"F0.imprint","IMPRINT",FACE,{"disambiguationData":[TD([[makeQuery(id+"F0.imprint","IMPRINT",EDGE,{"derivedFrom":subQ1}),1.0]])]});}
            var Q60;
            {var subQ1=sQuery(id+"F0.wireOp",EDGE,"E5.32.0");Q60=makeQuery(id+"F0.imprint","IMPRINT",FACE,{"disambiguationData":[TD([[makeQuery(id+"F0.imprint","IMPRINT",EDGE,{"derivedFrom":subQ1}),1.0]])]});}
            var Q61;
            {var subQ1=sQuery(id+"F0.wireOp",EDGE,"E5.30.0");Q61=makeQuery(id+"F0.imprint","IMPRINT",FACE,{"disambiguationData":[TD([[makeQuery(id+"F0.imprint","IMPRINT",EDGE,{"derivedFrom":subQ1}),1.0]])]});}
            var Q62;
            {var subQ1=sQuery(id+"F0.wireOp",EDGE,"E5.96.0");Q62=makeQuery(id+"F0.imprint","IMPRINT",FACE,{"disambiguationData":[TD([[makeQuery(id+"F0.imprint","IMPRINT",EDGE,{"derivedFrom":subQ1}),1.0]])]});}
            var Q63;
            {var subQ1=sQuery(id+"F0.wireOp",EDGE,"E5.5.0");Q63=makeQuery(id+"F0.imprint","IMPRINT",FACE,{"disambiguationData":[TD([[makeQuery(id+"F0.imprint","IMPRINT",EDGE,{"derivedFrom":subQ1}),1.0]])]});}
            var Q64;
            {var subQ1=sQuery(id+"F0.wireOp",EDGE,"E5.33.0");Q64=makeQuery(id+"F0.imprint","IMPRINT",FACE,{"disambiguationData":[TD([[makeQuery(id+"F0.imprint","IMPRINT",EDGE,{"derivedFrom":subQ1}),1.0]])]});}
            var Q65;
            {var subQ1=sQuery(id+"F0.wireOp",EDGE,"E5.34.0");Q65=makeQuery(id+"F0.imprint","IMPRINT",FACE,{"disambiguationData":[TD([[makeQuery(id+"F0.imprint","IMPRINT",EDGE,{"derivedFrom":subQ1}),1.0]])]});}
            var Q66;
            {var subQ1=sQuery(id+"F0.wireOp",EDGE,"E5.99.0");Q66=makeQuery(id+"F0.imprint","IMPRINT",FACE,{"disambiguationData":[TD([[makeQuery(id+"F0.imprint","IMPRINT",EDGE,{"derivedFrom":subQ1}),1.0]])]});}
            var Q67;
            {var subQ1=sQuery(id+"F0.wireOp",EDGE,"E5.31.0");Q67=makeQuery(id+"F0.imprint","IMPRINT",FACE,{"disambiguationData":[TD([[makeQuery(id+"F0.imprint","IMPRINT",EDGE,{"derivedFrom":subQ1}),1.0]])]});}
            var Q68;
            {var subQ1=sQuery(id+"F0.wireOp",EDGE,"E5.93.0");Q68=makeQuery(id+"F0.imprint","IMPRINT",FACE,{"disambiguationData":[TD([[makeQuery(id+"F0.imprint","IMPRINT",EDGE,{"derivedFrom":subQ1}),1.0]])]});}
            var Q69;
            {var subQ0=sQuery(id+"F0.wireOp",EDGE,"E5.92.0");Q69=makeQuery(id+"F0.imprint","IMPRINT",FACE,{"disambiguationData":[TD([[makeQuery(id+"F0.imprint","IMPRINT",EDGE,{"derivedFrom":subQ0}),1.0]])]});}
            var Q70;
            {var subQ1=sQuery(id+"F0.wireOp",EDGE,"E5.91.0");Q70=makeQuery(id+"F0.imprint","IMPRINT",FACE,{"disambiguationData":[TD([[makeQuery(id+"F0.imprint","IMPRINT",EDGE,{"derivedFrom":subQ1}),1.0]])]});}
            var Q71;
            {var subQ1=sQuery(id+"F0.wireOp",EDGE,"E5.90.0");Q71=makeQuery(id+"F0.imprint","IMPRINT",FACE,{"disambiguationData":[TD([[makeQuery(id+"F0.imprint","IMPRINT",EDGE,{"derivedFrom":subQ1}),1.0]])]});}
            var Q72;
            {var subQ0=sQuery(id+"F0.wireOp",EDGE,"E5.88.0");Q72=makeQuery(id+"F0.imprint","IMPRINT",FACE,{"disambiguationData":[TD([[makeQuery(id+"F0.imprint","IMPRINT",EDGE,{"derivedFrom":subQ0}),1.0]])]});}
            var Q73;
            {var subQ1=sQuery(id+"F0.wireOp",EDGE,"E5.86.0");Q73=makeQuery(id+"F0.imprint","IMPRINT",FACE,{"disambiguationData":[TD([[makeQuery(id+"F0.imprint","IMPRINT",EDGE,{"derivedFrom":subQ1}),1.0]])]});}
            var Q74;
            {var subQ1=sQuery(id+"F0.wireOp",EDGE,"E5.97.0");Q74=makeQuery(id+"F0.imprint","IMPRINT",FACE,{"disambiguationData":[TD([[makeQuery(id+"F0.imprint","IMPRINT",EDGE,{"derivedFrom":subQ1}),1.0]])]});}
            var Q75;
            {var subQ1=sQuery(id+"F0.wireOp",EDGE,"E5.98.0");Q75=makeQuery(id+"F0.imprint","IMPRINT",FACE,{"disambiguationData":[TD([[makeQuery(id+"F0.imprint","IMPRINT",EDGE,{"derivedFrom":subQ1}),1.0]])]});}
            var Q76;
            {var subQ1=sQuery(id+"F0.wireOp",EDGE,"E7.2.101.0");Q76=makeQuery(id+"F0.imprint","IMPRINT",FACE,{"disambiguationData":[TD([[makeQuery(id+"F0.imprint","IMPRINT",EDGE,{"derivedFrom":subQ1}),1.0]])]});}
            var Q77;
            {var subQ1=sQuery(id+"F0.wireOp",EDGE,"E7.2.102.0");Q77=makeQuery(id+"F0.imprint","IMPRINT",FACE,{"disambiguationData":[TD([[makeQuery(id+"F0.imprint","IMPRINT",EDGE,{"derivedFrom":subQ1}),1.0]])]});}
            var Q78;
            {var subQ1=sQuery(id+"F0.wireOp",EDGE,"E7.2.103.0");Q78=makeQuery(id+"F0.imprint","IMPRINT",FACE,{"disambiguationData":[TD([[makeQuery(id+"F0.imprint","IMPRINT",EDGE,{"derivedFrom":subQ1}),1.0]])]});}
            var Q79;
            {var subQ1=sQuery(id+"F0.wireOp",EDGE,"E5.85.0");Q79=makeQuery(id+"F0.imprint","IMPRINT",FACE,{"disambiguationData":[TD([[makeQuery(id+"F0.imprint","IMPRINT",EDGE,{"derivedFrom":subQ1}),1.0]])]});}
            var Q80;
            {var subQ1=sQuery(id+"F0.wireOp",EDGE,"E5.83.0");Q80=makeQuery(id+"F0.imprint","IMPRINT",FACE,{"disambiguationData":[TD([[makeQuery(id+"F0.imprint","IMPRINT",EDGE,{"derivedFrom":subQ1}),1.0]])]});}
            var Q81;
            {var subQ1=sQuery(id+"F0.wireOp",EDGE,"E5.82.0");Q81=makeQuery(id+"F0.imprint","IMPRINT",FACE,{"disambiguationData":[TD([[makeQuery(id+"F0.imprint","IMPRINT",EDGE,{"derivedFrom":subQ1}),1.0]])]});}
            var Q82;
            {var subQ1=sQuery(id+"F0.wireOp",EDGE,"E5.77.0");Q82=makeQuery(id+"F0.imprint","IMPRINT",FACE,{"disambiguationData":[TD([[makeQuery(id+"F0.imprint","IMPRINT",EDGE,{"derivedFrom":subQ1}),1.0]])]});}
            var Q83;
            {var subQ1=sQuery(id+"F0.wireOp",EDGE,"E5.75.0");Q83=makeQuery(id+"F0.imprint","IMPRINT",FACE,{"disambiguationData":[TD([[makeQuery(id+"F0.imprint","IMPRINT",EDGE,{"derivedFrom":subQ1}),1.0]])]});}
            var Q84;
            {var subQ1=sQuery(id+"F0.wireOp",EDGE,"E5.74.0");Q84=makeQuery(id+"F0.imprint","IMPRINT",FACE,{"disambiguationData":[TD([[makeQuery(id+"F0.imprint","IMPRINT",EDGE,{"derivedFrom":subQ1}),1.0]])]});}
            var Q85;
            {var subQ1=sQuery(id+"F0.wireOp",EDGE,"E5.73.0");Q85=makeQuery(id+"F0.imprint","IMPRINT",FACE,{"disambiguationData":[TD([[makeQuery(id+"F0.imprint","IMPRINT",EDGE,{"derivedFrom":subQ1}),1.0]])]});}
            var Q86;
            {var subQ1=sQuery(id+"F0.wireOp",EDGE,"E5.71.0");Q86=makeQuery(id+"F0.imprint","IMPRINT",FACE,{"disambiguationData":[TD([[makeQuery(id+"F0.imprint","IMPRINT",EDGE,{"derivedFrom":subQ1}),1.0]])]});}
            var Q87;
            {var subQ1=sQuery(id+"F0.wireOp",EDGE,"E5.70.0");Q87=makeQuery(id+"F0.imprint","IMPRINT",FACE,{"disambiguationData":[TD([[makeQuery(id+"F0.imprint","IMPRINT",EDGE,{"derivedFrom":subQ1}),1.0]])]});}
            var Q88;
            {var subQ1=sQuery(id+"F0.wireOp",EDGE,"E5.67.0");Q88=makeQuery(id+"F0.imprint","IMPRINT",FACE,{"disambiguationData":[TD([[makeQuery(id+"F0.imprint","IMPRINT",EDGE,{"derivedFrom":subQ1}),1.0]])]});}
            var Q89;
            {var subQ1=sQuery(id+"F0.wireOp",EDGE,"E5.66.0");Q89=makeQuery(id+"F0.imprint","IMPRINT",FACE,{"disambiguationData":[TD([[makeQuery(id+"F0.imprint","IMPRINT",EDGE,{"derivedFrom":subQ1}),1.0]])]});}
            var Q90;
            {var subQ1=sQuery(id+"F0.wireOp",EDGE,"E5.65.0");Q90=makeQuery(id+"F0.imprint","IMPRINT",FACE,{"disambiguationData":[TD([[makeQuery(id+"F0.imprint","IMPRINT",EDGE,{"derivedFrom":subQ1}),1.0]])]});}
            var Q91;
            {var subQ1=sQuery(id+"F0.wireOp",EDGE,"E5.64.0");Q91=makeQuery(id+"F0.imprint","IMPRINT",FACE,{"disambiguationData":[TD([[makeQuery(id+"F0.imprint","IMPRINT",EDGE,{"derivedFrom":subQ1}),1.0]])]});}
            var Q92;
            {var subQ1=sQuery(id+"F0.wireOp",EDGE,"E5.60.0");Q92=makeQuery(id+"F0.imprint","IMPRINT",FACE,{"disambiguationData":[TD([[makeQuery(id+"F0.imprint","IMPRINT",EDGE,{"derivedFrom":subQ1}),1.0]])]});}
            var Q93;
            {var subQ1=sQuery(id+"F0.wireOp",EDGE,"E5.59.0");Q93=makeQuery(id+"F0.imprint","IMPRINT",FACE,{"disambiguationData":[TD([[makeQuery(id+"F0.imprint","IMPRINT",EDGE,{"derivedFrom":subQ1}),1.0]])]});}
            var Q94;
            {var subQ1=sQuery(id+"F0.wireOp",EDGE,"E5.57.0");Q94=makeQuery(id+"F0.imprint","IMPRINT",FACE,{"disambiguationData":[TD([[makeQuery(id+"F0.imprint","IMPRINT",EDGE,{"derivedFrom":subQ1}),1.0]])]});}
            var Q95;
            {var subQ1=sQuery(id+"F0.wireOp",EDGE,"E5.55.0");Q95=makeQuery(id+"F0.imprint","IMPRINT",FACE,{"disambiguationData":[TD([[makeQuery(id+"F0.imprint","IMPRINT",EDGE,{"derivedFrom":subQ1}),1.0]])]});}
            var Q96;
            {var subQ1=sQuery(id+"F0.wireOp",EDGE,"E5.49.0");Q96=makeQuery(id+"F0.imprint","IMPRINT",FACE,{"disambiguationData":[TD([[makeQuery(id+"F0.imprint","IMPRINT",EDGE,{"derivedFrom":subQ1}),1.0]])]});}
            var Q97;
            {var subQ1=sQuery(id+"F0.wireOp",EDGE,"E5.48.0");Q97=makeQuery(id+"F0.imprint","IMPRINT",FACE,{"disambiguationData":[TD([[makeQuery(id+"F0.imprint","IMPRINT",EDGE,{"derivedFrom":subQ1}),1.0]])]});}
            var Q98;
            {var subQ1=sQuery(id+"F0.wireOp",EDGE,"E5.45.0");Q98=makeQuery(id+"F0.imprint","IMPRINT",FACE,{"disambiguationData":[TD([[makeQuery(id+"F0.imprint","IMPRINT",EDGE,{"derivedFrom":subQ1}),1.0]])]});}
            var Q99;
            {var subQ1=sQuery(id+"F0.wireOp",EDGE,"E5.44.0");Q99=makeQuery(id+"F0.imprint","IMPRINT",FACE,{"disambiguationData":[TD([[makeQuery(id+"F0.imprint","IMPRINT",EDGE,{"derivedFrom":subQ1}),1.0]])]});}
            var Q100;
            {var subQ1=sQuery(id+"F0.wireOp",EDGE,"E5.42.0");Q100=makeQuery(id+"F0.imprint","IMPRINT",FACE,{"disambiguationData":[TD([[makeQuery(id+"F0.imprint","IMPRINT",EDGE,{"derivedFrom":subQ1}),1.0]])]});}
            var Q101;
            {var subQ1=sQuery(id+"F0.wireOp",EDGE,"E5.40.0");Q101=makeQuery(id+"F0.imprint","IMPRINT",FACE,{"disambiguationData":[TD([[makeQuery(id+"F0.imprint","IMPRINT",EDGE,{"derivedFrom":subQ1}),1.0]])]});}
            var Q102;
            {var subQ0=sQuery(id+"F0.wireOp",EDGE,"E5.39.0");Q102=makeQuery(id+"F0.imprint","IMPRINT",FACE,{"disambiguationData":[TD([[makeQuery(id+"F0.imprint","IMPRINT",EDGE,{"derivedFrom":subQ0}),1.0]])]});}
            var Q103;
            {var subQ1=sQuery(id+"F0.wireOp",EDGE,"E5.37.0");Q103=makeQuery(id+"F0.imprint","IMPRINT",FACE,{"disambiguationData":[TD([[makeQuery(id+"F0.imprint","IMPRINT",EDGE,{"derivedFrom":subQ1}),1.0]])]});}
            var Q104;
            {var subQ1=sQuery(id+"F0.wireOp",EDGE,"E5.29.0");Q104=makeQuery(id+"F0.imprint","IMPRINT",FACE,{"disambiguationData":[TD([[makeQuery(id+"F0.imprint","IMPRINT",EDGE,{"derivedFrom":subQ1}),1.0]])]});}
            var Q105;
            {var subQ1=sQuery(id+"F0.wireOp",EDGE,"E5.28.0");Q105=makeQuery(id+"F0.imprint","IMPRINT",FACE,{"disambiguationData":[TD([[makeQuery(id+"F0.imprint","IMPRINT",EDGE,{"derivedFrom":subQ1}),1.0]])]});}
            var Q106;
            {var subQ1=sQuery(id+"F0.wireOp",EDGE,"E5.23.0");Q106=makeQuery(id+"F0.imprint","IMPRINT",FACE,{"disambiguationData":[TD([[makeQuery(id+"F0.imprint","IMPRINT",EDGE,{"derivedFrom":subQ1}),1.0]])]});}
            var Q107;
            {var subQ1=sQuery(id+"F0.wireOp",EDGE,"E5.22.0");Q107=makeQuery(id+"F0.imprint","IMPRINT",FACE,{"disambiguationData":[TD([[makeQuery(id+"F0.imprint","IMPRINT",EDGE,{"derivedFrom":subQ1}),1.0]])]});}
            var Q108;
            {var subQ1=sQuery(id+"F0.wireOp",EDGE,"E5.21.0");Q108=makeQuery(id+"F0.imprint","IMPRINT",FACE,{"disambiguationData":[TD([[makeQuery(id+"F0.imprint","IMPRINT",EDGE,{"derivedFrom":subQ1}),1.0]])]});}
            var Q109;
            {var subQ1=sQuery(id+"F0.wireOp",EDGE,"E5.19.0");Q109=makeQuery(id+"F0.imprint","IMPRINT",FACE,{"disambiguationData":[TD([[makeQuery(id+"F0.imprint","IMPRINT",EDGE,{"derivedFrom":subQ1}),1.0]])]});}
            var Q110;
            {var subQ1=sQuery(id+"F0.wireOp",EDGE,"E5.14.0");Q110=makeQuery(id+"F0.imprint","IMPRINT",FACE,{"disambiguationData":[TD([[makeQuery(id+"F0.imprint","IMPRINT",EDGE,{"derivedFrom":subQ1}),1.0]])]});}
            var Q111;
            {var subQ1=sQuery(id+"F0.wireOp",EDGE,"E5.13.0");Q111=makeQuery(id+"F0.imprint","IMPRINT",FACE,{"disambiguationData":[TD([[makeQuery(id+"F0.imprint","IMPRINT",EDGE,{"derivedFrom":subQ1}),1.0]])]});}
            var Q112;
            {var subQ0=sQuery(id+"F0.wireOp",EDGE,"E5.11.0");Q112=makeQuery(id+"F0.imprint","IMPRINT",FACE,{"disambiguationData":[TD([[makeQuery(id+"F0.imprint","IMPRINT",EDGE,{"derivedFrom":subQ0}),1.0]])]});}
            var Q113;
            {var subQ1=sQuery(id+"F0.wireOp",EDGE,"E5.10.0");Q113=makeQuery(id+"F0.imprint","IMPRINT",FACE,{"disambiguationData":[TD([[makeQuery(id+"F0.imprint","IMPRINT",EDGE,{"derivedFrom":subQ1}),1.0]])]});}
            var Q114;
            {var subQ0=sQuery(id+"F0.wireOp",EDGE,"E5.9.0");Q114=makeQuery(id+"F0.imprint","IMPRINT",FACE,{"disambiguationData":[TD([[makeQuery(id+"F0.imprint","IMPRINT",EDGE,{"derivedFrom":subQ0}),1.0]])]});}
            var Q115;
            {var subQ1=sQuery(id+"F0.wireOp",EDGE,"E5.7.0");Q115=makeQuery(id+"F0.imprint","IMPRINT",FACE,{"disambiguationData":[TD([[makeQuery(id+"F0.imprint","IMPRINT",EDGE,{"derivedFrom":subQ1}),1.0]])]});}
            var Q116;
            {var subQ1=sQuery(id+"F0.wireOp",EDGE,"E5.6.0");Q116=makeQuery(id+"F0.imprint","IMPRINT",FACE,{"disambiguationData":[TD([[makeQuery(id+"F0.imprint","IMPRINT",EDGE,{"derivedFrom":subQ1}),1.0]])]});}
            var Q117;
            {var subQ1=sQuery(id+"F0.wireOp",EDGE,"E5.4.0");Q117=makeQuery(id+"F0.imprint","IMPRINT",FACE,{"disambiguationData":[TD([[makeQuery(id+"F0.imprint","IMPRINT",EDGE,{"derivedFrom":subQ1}),1.0]])]});}
            var Q118;
            {var subQ1=sQuery(id+"F0.wireOp",EDGE,"E2");Q118=makeQuery(id+"F0.imprint","IMPRINT",FACE,{"disambiguationData":[TD([[makeQuery(id+"F0.imprint","IMPRINT",EDGE,{"derivedFrom":subQ1}),1.0]])]});}
            var Q119;
            {var subQ1=sQuery(id+"F0.wireOp",EDGE,"E7.2.105.0");Q119=makeQuery(id+"F0.imprint","IMPRINT",FACE,{"disambiguationData":[TD([[makeQuery(id+"F0.imprint","IMPRINT",EDGE,{"derivedFrom":subQ1}),1.0]])]});}
            var Q120;
            {var subQ1=sQuery(id+"F0.wireOp",EDGE,"E7.2.107.0");Q120=makeQuery(id+"F0.imprint","IMPRINT",FACE,{"disambiguationData":[TD([[makeQuery(id+"F0.imprint","IMPRINT",EDGE,{"derivedFrom":subQ1}),1.0]])]});}
            var Q121;
            {var subQ1=sQuery(id+"F0.wireOp",EDGE,"E7.2.109.0");Q121=makeQuery(id+"F0.imprint","IMPRINT",FACE,{"disambiguationData":[TD([[makeQuery(id+"F0.imprint","IMPRINT",EDGE,{"derivedFrom":subQ1}),1.0]])]});}
            var Q122;
            {var subQ1=sQuery(id+"F0.wireOp",EDGE,"E7.2.110.0");Q122=makeQuery(id+"F0.imprint","IMPRINT",FACE,{"disambiguationData":[TD([[makeQuery(id+"F0.imprint","IMPRINT",EDGE,{"derivedFrom":subQ1}),1.0]])]});}
            var Q123;
            {var subQ1=sQuery(id+"F0.wireOp",EDGE,"E7.2.113.0");Q123=makeQuery(id+"F0.imprint","IMPRINT",FACE,{"disambiguationData":[TD([[makeQuery(id+"F0.imprint","IMPRINT",EDGE,{"derivedFrom":subQ1}),1.0]])]});}
            var Q124;
            {var subQ1=sQuery(id+"F0.wireOp",EDGE,"E7.2.116.0");Q124=makeQuery(id+"F0.imprint","IMPRINT",FACE,{"disambiguationData":[TD([[makeQuery(id+"F0.imprint","IMPRINT",EDGE,{"derivedFrom":subQ1}),1.0]])]});}
            var Q125;
            {var subQ1=sQuery(id+"F0.wireOp",EDGE,"E7.2.121.0");Q125=makeQuery(id+"F0.imprint","IMPRINT",FACE,{"disambiguationData":[TD([[makeQuery(id+"F0.imprint","IMPRINT",EDGE,{"derivedFrom":subQ1}),1.0]])]});}
            var Q126;
            {var subQ1=sQuery(id+"F0.wireOp",EDGE,"E7.2.119.0");Q126=makeQuery(id+"F0.imprint","IMPRINT",FACE,{"disambiguationData":[TD([[makeQuery(id+"F0.imprint","IMPRINT",EDGE,{"derivedFrom":subQ1}),1.0]])]});}
            var Q127;
            {var subQ1=sQuery(id+"F0.wireOp",EDGE,"E7.2.123.0");Q127=makeQuery(id+"F0.imprint","IMPRINT",FACE,{"disambiguationData":[TD([[makeQuery(id+"F0.imprint","IMPRINT",EDGE,{"derivedFrom":subQ1}),1.0]])]});}
            var Q128;
            {var subQ1=sQuery(id+"F0.wireOp",EDGE,"E7.2.124.0");Q128=makeQuery(id+"F0.imprint","IMPRINT",FACE,{"disambiguationData":[TD([[makeQuery(id+"F0.imprint","IMPRINT",EDGE,{"derivedFrom":subQ1}),1.0]])]});}
            var Q129;
            {var subQ1=sQuery(id+"F0.wireOp",EDGE,"E7.2.125.0");Q129=makeQuery(id+"F0.imprint","IMPRINT",FACE,{"disambiguationData":[TD([[makeQuery(id+"F0.imprint","IMPRINT",EDGE,{"derivedFrom":subQ1}),1.0]])]});}
            var Q130;
            {var subQ1=sQuery(id+"F0.wireOp",EDGE,"E7.2.126.0");Q130=makeQuery(id+"F0.imprint","IMPRINT",FACE,{"disambiguationData":[TD([[makeQuery(id+"F0.imprint","IMPRINT",EDGE,{"derivedFrom":subQ1}),1.0]])]});}
            extrude(context, id + "F1", {"entities" : qUnion([Q0, Q1, Q2, Q3, Q4, Q5, Q6, Q7, Q8, Q9, Q10, Q11, Q12, Q13, Q14, Q15, Q16, Q17, Q18, Q19, Q20, Q21, Q22, Q23, Q24, Q25, Q26, Q27, Q28, Q29, Q30, Q31, Q32, Q33, Q34, Q35, Q36, Q37, Q38, Q39, Q40, Q41, Q42, Q43, Q44, Q45, Q46, Q47, Q48, Q49, Q50, Q51, Q52, Q53, Q54, Q55, Q56, Q57, Q58, Q59, Q60, Q61, Q62, Q63, Q64, Q65, Q66, Q67, Q68, Q69, Q70, Q71, Q72, Q73, Q74, Q75, Q76, Q77, Q78, Q79, Q80, Q81, Q82, Q83, Q84, Q85, Q86, Q87, Q88, Q89, Q90, Q91, Q92, Q93, Q94, Q95, Q96, Q97, Q98, Q99, Q100, Q101, Q102, Q103, Q104, Q105, Q106, Q107, Q108, Q109, Q110, Q111, Q112, Q113, Q114, Q115, Q116, Q117, Q118, Q119, Q120, Q121, Q122, Q123, Q124, Q125, Q126, Q127, Q128, Q129, Q130]), "depth" : 1 * mm});
        }
    });
